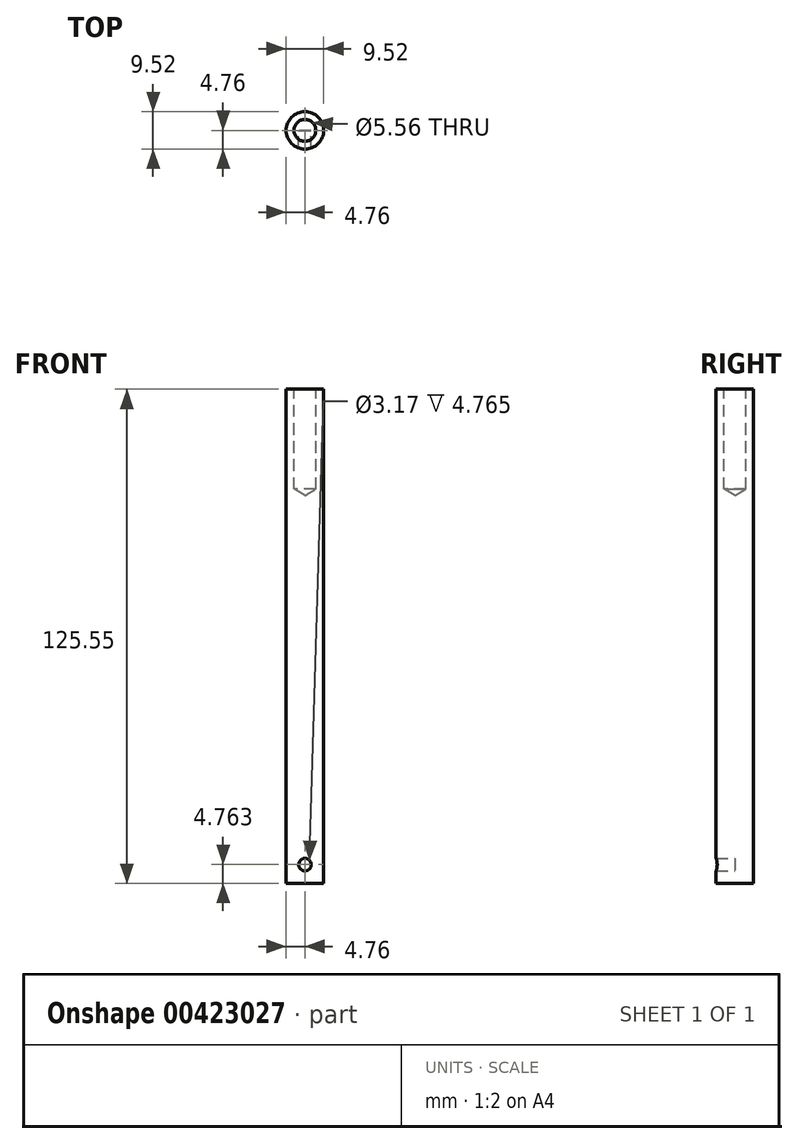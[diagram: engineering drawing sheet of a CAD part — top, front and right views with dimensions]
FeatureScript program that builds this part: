
annotation { "Feature Type Name" : "Feature", "Feature Type Description" : "" }
export const myFeature = defineFeature(function(context is Context, id is Id, definition is map)
    precondition{}
    {
        {
            var Q0;
            Q0=qCreatedBy(makeId("Top.planeOp"),FACE);
            var sketch = newSketch(context, id + "F0", { "sketchPlane" : qUnion([Q0])});
            skCircle(sketch, "E0", {"center": v(0, 0) * mm, "radius": 4.76 * mm});
            skSolve(sketch);
        }
        {
            var Q0;
            Q0=qSketchRegion(id+"F0",true);
            extrude(context, id + "F1", {"entities" : qUnion([Q0]), "depth" : 125.55 * mm});
        }
        {
            var Q0;
            Q0=qCreatedBy(makeId("Front.planeOp"),FACE);
            var sketch = newSketch(context, id + "F2", { "sketchPlane" : qUnion([Q0])});
            skPoint(sketch, "E1", {"position": v(0, 4.76) * mm});
            skSolve(sketch);
        }
        {
            var Q0;
            Q0=sQuery(id+"F2.wireOp",VERTEX,"E1");
            var Q1;
            Q1=makeQuery(id+"F1.opExtrude","SWEPT_BODY",BODY,{"disambiguationData":[OSD([sQuery(id+"F0.wireOp",EDGE,"E0")])]});
            hole(context, id + "F3", {"style" : HoleStyle.C_BORE, "endStyle" : HoleEndStyle.BLIND, "oppositeDirection" : true, "holeDiameter" : 3.17 * mm, "cBoreDiameter" : 3.17 * mm, "cBoreDepth" : 6.35 * mm, "holeDepth" : 16.5 * mm, "isTappedThrough" : true, "tappedDepth" : 12.7 * mm, "tapClearance" : 3, "locations" : qUnion([Q0]), "scope" : qUnion([Q1])});
        }
        {
            var Q0;
            Q0=makeQuery(id+"F1.opExtrude","CAP_FACE",FACE,{"disambiguationData":[OSD([sQuery(id+"F0.wireOp",EDGE,"E0")])],"isStart":false});
            var sketch = newSketch(context, id + "F4", { "sketchPlane" : qUnion([Q0])});
            skPoint(sketch, "E2", {"position": v(0, 0) * mm});
            skSolve(sketch);
        }
        {
            var Q0;
            Q0=sQuery(id+"F4.wireOp",VERTEX,"E2");
            var Q1;
            Q1=makeQuery(id+"F1.opExtrude","SWEPT_BODY",BODY,{"disambiguationData":[OSD([sQuery(id+"F0.wireOp",EDGE,"E0")])]});
            hole(context, id + "F5", {"style" : HoleStyle.C_BORE, "endStyle" : HoleEndStyle.BLIND, "holeDiameter" : 5.56 * mm, "cBoreDiameter" : 5.56 * mm, "cBoreDepth" : 6.35 * mm, "holeDepth" : 25.4 * mm, "isTappedThrough" : true, "tappedDepth" : 12.7 * mm, "tapClearance" : 3, "locations" : qUnion([Q0]), "scope" : qUnion([Q1])});
        }
    });
